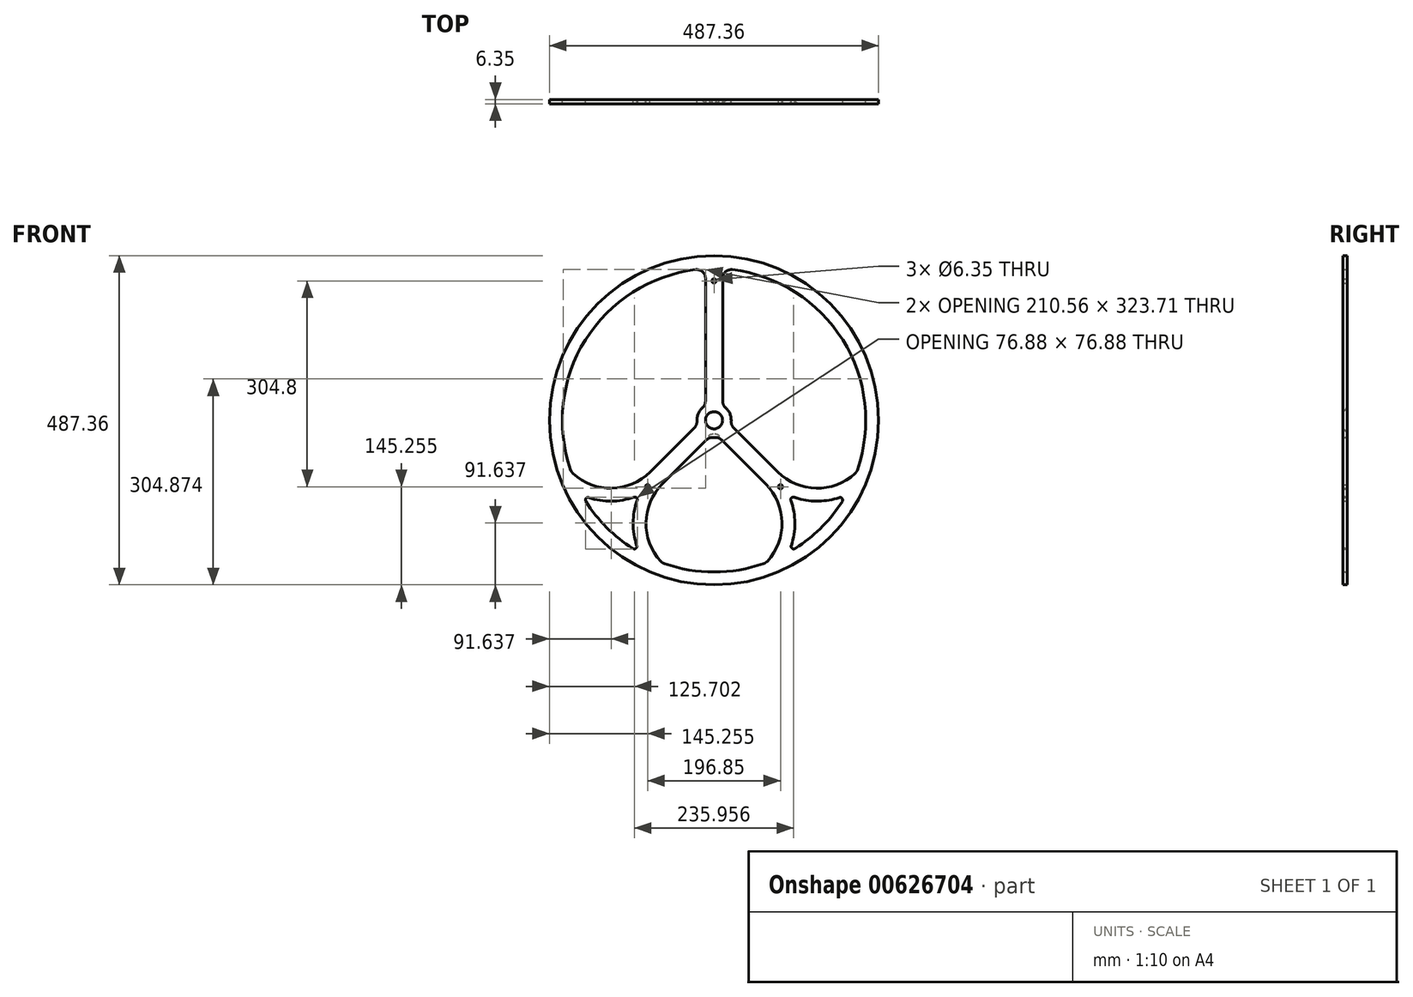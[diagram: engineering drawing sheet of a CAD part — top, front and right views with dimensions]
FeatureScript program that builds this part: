
annotation { "Feature Type Name" : "Feature", "Feature Type Description" : "" }
export const myFeature = defineFeature(function(context is Context, id is Id, definition is map)
    precondition{}
    {
        {
            var Q0;
            Q0=qCreatedBy(makeId("Front.planeOp"),FACE);
            var sketch = newSketch(context, id + "F0", { "sketchPlane" : qUnion([Q0])});
            skCircle(sketch, "E0", {"center": v(0, 0) * mm, "radius": 243.68 * mm});
            skArc(sketch, "E1", {"start": v(-12.7, 224.27) * mm, "mid": v(-187.48, 123.73) * mm, "end": v(-211.2, -76.5) * mm});
            skArc(sketch, "E2", {"start": v(-12.7, 22) * mm, "mid": v(-23.47, 9.72) * mm, "end": v(-24.53, -6.57) * mm});
            skCircle(sketch, "E3", {"center": v(0, 0) * mm, "radius": 12.7 * mm});
            skLineSegment(sketch, "E4", {"start": v(0, 267.5) * mm, "end": v(0, -275.56) * mm, "construction": true});
            skLineSegment(sketch, "E5", {"start": v(0, 0) * mm, "end": v(-264.17, -264.17) * mm, "construction": true});
            skLineSegment(sketch, "E6", {"start": v(0, 0) * mm, "end": v(264.17, -264.17) * mm, "construction": true});
            skLineSegment(sketch, "E7", {"start": v(-12.7, 224.27) * mm, "end": v(-12.7, 22) * mm});
            skLineSegment(sketch, "E8", {"start": v(12.7, 224.27) * mm, "end": v(12.7, 22) * mm});
            skArc(sketch, "E9.trimOffspring", {"start": v(24.53, -6.57) * mm, "mid": v(23.47, 9.72) * mm, "end": v(12.7, 22) * mm});
            skArc(sketch, "E10.trimOffspring", {"start": v(-6.57, -24.53) * mm, "mid": v(0, -25.4) * mm, "end": v(6.57, -24.53) * mm});
            skArc(sketch, "E11.trimOffspring", {"start": v(-195.73, -110.23) * mm, "mid": v(-158.84, -158.84) * mm, "end": v(-110.23, -195.73) * mm});
            skArc(sketch, "E12.trimOffspring", {"start": v(211.2, -76.5) * mm, "mid": v(187.48, 123.73) * mm, "end": v(12.7, 224.27) * mm});
            skCircle(sketch, "E13", {"center": v(0, 206.38) * mm, "radius": 3.18 * mm});
            skCircle(sketch, "E14", {"center": v(-98.42, -98.43) * mm, "radius": 3.18 * mm});
            skCircle(sketch, "E15", {"center": v(98.43, -98.43) * mm, "radius": 3.18 * mm});
            skLineSegment(sketch, "E16", {"start": v(-24.53, -6.57) * mm, "end": v(-94.46, -76.5) * mm});
            skLineSegment(sketch, "E17", {"start": v(-6.57, -24.53) * mm, "end": v(-76.5, -94.46) * mm});
            skLineSegment(sketch, "E18", {"start": v(24.53, -6.57) * mm, "end": v(94.46, -76.5) * mm});
            skLineSegment(sketch, "E19", {"start": v(6.57, -24.53) * mm, "end": v(76.5, -94.46) * mm});
            skLineSegment(sketch, "E20", {"start": v(148.79, 51.47) * mm, "end": v(152.93, 40.82) * mm});
            skArc(sketch, "E21", {"start": v(-211.2, -76.5) * mm, "mid": v(-152.83, -100.68) * mm, "end": v(-94.46, -76.5) * mm});
            skArc(sketch, "E22", {"start": v(-76.5, -94.46) * mm, "mid": v(-100.68, -152.83) * mm, "end": v(-76.5, -211.2) * mm});
            skArc(sketch, "E23", {"start": v(76.5, -211.2) * mm, "mid": v(100.68, -152.83) * mm, "end": v(76.5, -94.46) * mm});
            skArc(sketch, "E24", {"start": v(94.46, -76.5) * mm, "mid": v(152.83, -100.68) * mm, "end": v(211.2, -76.5) * mm});
            skArc(sketch, "E25", {"start": v(-110.48, -110.48) * mm, "mid": v(-119.73, -153.13) * mm, "end": v(-110.23, -195.73) * mm});
            skArc(sketch, "E26", {"start": v(110.23, -195.73) * mm, "mid": v(119.73, -153.13) * mm, "end": v(110.48, -110.48) * mm});
            skArc(sketch, "E27.trimOffspring", {"start": v(-76.5, -211.2) * mm, "mid": v(0, -224.63) * mm, "end": v(76.5, -211.2) * mm});
            skArc(sketch, "E28.trimOffspring", {"start": v(110.23, -195.73) * mm, "mid": v(158.84, -158.84) * mm, "end": v(195.73, -110.23) * mm});
            skArc(sketch, "E29", {"start": v(110.48, -110.48) * mm, "mid": v(153.13, -119.73) * mm, "end": v(195.73, -110.23) * mm});
            skArc(sketch, "E30", {"start": v(-195.73, -110.23) * mm, "mid": v(-153.13, -119.73) * mm, "end": v(-110.48, -110.48) * mm});
            skLineSegment(sketch, "E31", {"start": v(0, 0) * mm, "end": v(110.48, -110.48) * mm});
            skSolve(sketch);
        }
        {
            var Q0;
            Q0=makeQuery(id+"F0.imprint","IMPRINT",FACE,{"disambiguationData":[TD([[makeQuery(id+"F0.imprint","IMPRINT",EDGE,{"derivedFrom":sQuery(id+"F0.wireOp",EDGE,"E0")}),1.0]])]});
            var Q1;
            Q1=sQuery(id+"F0.wireOp",EDGE,"E1");
            var Q2;
            Q2=sQuery(id+"F0.wireOp",EDGE,"E0");
            var Q3;
            Q3=sQuery(id+"F0.wireOp",EDGE,"E12.trimOffspring");
            var Q4;
            Q4=sQuery(id+"F0.wireOp",EDGE,"E9.trimOffspring");
            var Q5;
            Q5=sQuery(id+"F0.wireOp",EDGE,"E2");
            var Q6;
            Q6=sQuery(id+"F0.wireOp",EDGE,"E7");
            var Q7;
            Q7=sQuery(id+"F0.wireOp",EDGE,"E8");
            var Q8;
            Q8=sQuery(id+"F0.wireOp",EDGE,"E10.trimOffspring");
            var Q9;
            Q9=sQuery(id+"F0.wireOp",EDGE,"0MUlm2yo-4CSH-LrVN-fMGO-j9xlGpz9AVfv");
            var Q10;
            Q10=sQuery(id+"F0.wireOp",EDGE,"2eT3RHkh-0bmi-F0uN-6XSI-4qLjh6PCMfJx");
            var Q11;
            Q11=sQuery(id+"F0.wireOp",EDGE,"E11.trimOffspring");
            var Q12;
            Q12=sQuery(id+"F0.wireOp",EDGE,"0W93g2Ux-YMUG-o7GS-L5Pk-QG37dWORR4TO");
            var Q13;
            Q13=sQuery(id+"F0.wireOp",EDGE,"bBKFYuQ6-KArc-nRwX-f4Xk-UpNSekpAzjOm");
            var Q14;
            Q14=sQuery(id+"F0.wireOp",EDGE,"E3");
            extrude(context, id + "F1", {"entities" : qUnion([Q0]), "surfaceEntities" : qUnion([Q1, Q2, Q3, Q4, Q5, Q6, Q7, Q8, Q9, Q10, Q11, Q12, Q13, Q14]), "depth" : 6.35 * mm, "offsetDistance" : 25.4 * mm});
        }
        {
            var Q0;
            Q0=makeQuery(id+"F1.opExtrude","SWEPT_EDGE",EDGE,{"disambiguationData":[OSD([sQuery(id+"F0.wireOp",EDGE,"E8"),sQuery(id+"F0.wireOp",EDGE,"E12.trimOffspring")])]});
            var Q1;
            Q1=makeQuery(id+"F1.opExtrude","SWEPT_EDGE",EDGE,{"disambiguationData":[OSD([sQuery(id+"F0.wireOp",EDGE,"E1"),sQuery(id+"F0.wireOp",EDGE,"E7")])]});
            var Q2;
            Q2=makeQuery(id+"F1.opExtrude","SWEPT_EDGE",EDGE,{"disambiguationData":[OSD([sQuery(id+"F0.wireOp",EDGE,"E2"),sQuery(id+"F0.wireOp",EDGE,"E7")])]});
            var Q3;
            Q3=makeQuery(id+"F1.opExtrude","SWEPT_EDGE",EDGE,{"disambiguationData":[OSD([sQuery(id+"F0.wireOp",EDGE,"E2"),sQuery(id+"F0.wireOp",EDGE,"E16")])]});
            var Q4;
            Q4=makeQuery(id+"F1.opExtrude","SWEPT_EDGE",EDGE,{"disambiguationData":[OSD([sQuery(id+"F0.wireOp",EDGE,"E8"),sQuery(id+"F0.wireOp",EDGE,"E9.trimOffspring")])]});
            var Q5;
            Q5=makeQuery(id+"F1.opExtrude","SWEPT_EDGE",EDGE,{"disambiguationData":[OSD([sQuery(id+"F0.wireOp",EDGE,"E9.trimOffspring"),sQuery(id+"F0.wireOp",EDGE,"E18")])]});
            var Q6;
            Q6=makeQuery(id+"F1.opExtrude","CAP_EDGE",EDGE,{"disambiguationData":[OSD([sQuery(id+"F0.wireOp",EDGE,"E3")])],"isStart":true});
            var Q7;
            Q7=makeQuery(id+"F1.opExtrude","SWEPT_EDGE",EDGE,{"disambiguationData":[OSD([sQuery(id+"F0.wireOp",EDGE,"E10.trimOffspring"),sQuery(id+"F0.wireOp",EDGE,"E19")])]});
            var Q8;
            Q8=makeQuery(id+"F1.opExtrude","SWEPT_EDGE",EDGE,{"disambiguationData":[OSD([sQuery(id+"F0.wireOp",EDGE,"E10.trimOffspring"),sQuery(id+"F0.wireOp",EDGE,"E17")])]});
            var Q9;
            Q9=makeQuery(id+"F1.opExtrude","SWEPT_EDGE",EDGE,{"disambiguationData":[OSD([sQuery(id+"F0.wireOp",EDGE,"E22"),sQuery(id+"F0.wireOp",EDGE,"E27.trimOffspring")])]});
            var Q10;
            Q10=makeQuery(id+"F1.opExtrude","SWEPT_EDGE",EDGE,{"disambiguationData":[OSD([sQuery(id+"F0.wireOp",EDGE,"E1"),sQuery(id+"F0.wireOp",EDGE,"E21")])]});
            var Q11;
            Q11=makeQuery(id+"F1.opExtrude","SWEPT_EDGE",EDGE,{"disambiguationData":[OSD([sQuery(id+"F0.wireOp",EDGE,"E23"),sQuery(id+"F0.wireOp",EDGE,"E27.trimOffspring")])]});
            var Q12;
            Q12=makeQuery(id+"F1.opExtrude","SWEPT_EDGE",EDGE,{"disambiguationData":[OSD([sQuery(id+"F0.wireOp",EDGE,"E12.trimOffspring"),sQuery(id+"F0.wireOp",EDGE,"E24")])]});
            fillet(context, id + "F2", {"entities" : qUnion([Q0, Q1, Q2, Q3, Q4, Q5, Q6, Q7, Q8, Q9, Q10, Q11, Q12]), "radius" : 12.7 * mm, "tangentPropagation" : true, "allowEdgeOverflow" : false});
        }
        {
            var Q0;
            Q0=makeQuery(id+"F1.opExtrude","SWEPT_EDGE",EDGE,{"disambiguationData":[OSD([sQuery(id+"F0.wireOp",EDGE,"4ohm5EKj-daJ9-b2b6-KeMV-xKns7FrgNd51"),sQuery(id+"F0.wireOp",EDGE,"E25")])]});
            var Q1;
            Q1=makeQuery(id+"F1.opExtrude","SWEPT_EDGE",EDGE,{"disambiguationData":[OSD([sQuery(id+"F0.wireOp",EDGE,"E11.trimOffspring"),sQuery(id+"F0.wireOp",EDGE,"4ohm5EKj-daJ9-b2b6-KeMV-xKns7FrgNd51")])]});
            var Q2;
            Q2=makeQuery(id+"F1.opExtrude","SWEPT_EDGE",EDGE,{"disambiguationData":[OSD([sQuery(id+"F0.wireOp",EDGE,"E11.trimOffspring"),sQuery(id+"F0.wireOp",EDGE,"E25")])]});
            var Q3;
            Q3=makeQuery(id+"F1.opExtrude","SWEPT_EDGE",EDGE,{"disambiguationData":[OSD([sQuery(id+"F0.wireOp",EDGE,"E26"),sQuery(id+"F0.wireOp",EDGE,"E28.trimOffspring")])]});
            var Q4;
            Q4=makeQuery(id+"F1.opExtrude","SWEPT_EDGE",EDGE,{"disambiguationData":[OSD([sQuery(id+"F0.wireOp",EDGE,"iMYomyUU-eH3X-xzJJ-K4yo-Cazyb2Zp6VGt"),sQuery(id+"F0.wireOp",EDGE,"E28.trimOffspring")])]});
            var Q5;
            Q5=makeQuery(id+"F1.opExtrude","SWEPT_EDGE",EDGE,{"disambiguationData":[OSD([sQuery(id+"F0.wireOp",EDGE,"iMYomyUU-eH3X-xzJJ-K4yo-Cazyb2Zp6VGt"),sQuery(id+"F0.wireOp",EDGE,"E26")])]});
            var Q6;
            Q6=makeQuery(id+"F1.opExtrude","CAP_EDGE",EDGE,{"disambiguationData":[OSD([sQuery(id+"F0.wireOp",EDGE,"E10.trimOffspring")])],"isStart":true});
            var Q7;
            Q7=makeQuery(id+"F1.opExtrude","CAP_EDGE",EDGE,{"disambiguationData":[OSD([sQuery(id+"F0.wireOp",EDGE,"E26")])],"isStart":false});
            fillet(context, id + "F3", {"entities" : qUnion([Q0, Q1, Q2, Q3, Q4, Q5, Q6, Q7]), "radius" : 3.8 * mm, "tangentPropagation" : true, "allowEdgeOverflow" : false});
        }
    });
